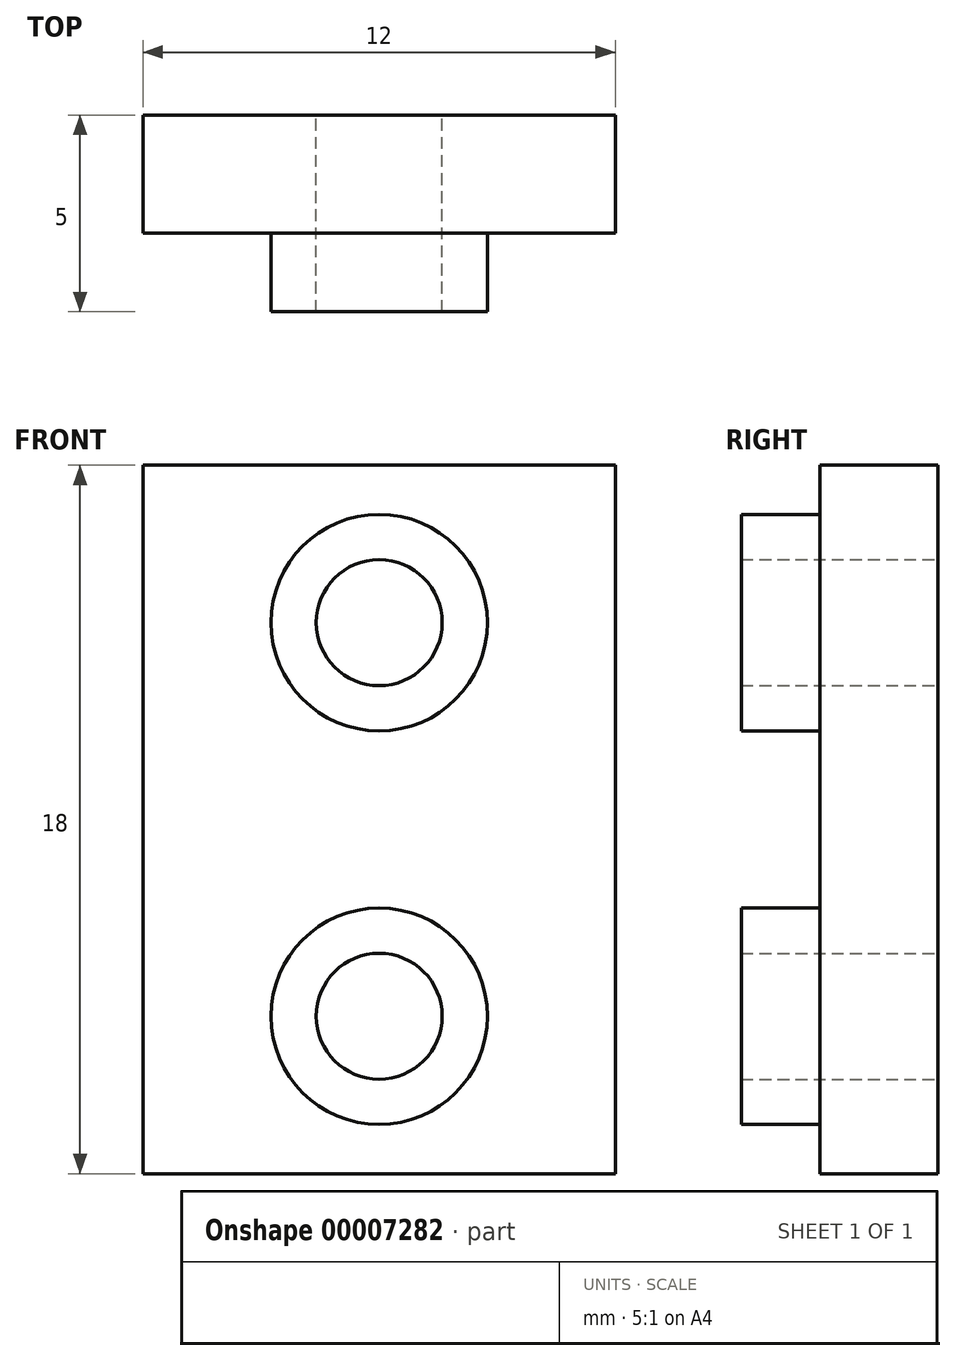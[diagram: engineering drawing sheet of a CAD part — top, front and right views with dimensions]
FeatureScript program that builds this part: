
annotation { "Feature Type Name" : "Feature", "Feature Type Description" : "" }
export const myFeature = defineFeature(function(context is Context, id is Id, definition is map)
    precondition{}
    {
        {
            var Q0;
            Q0=qCreatedBy(makeId("Front.planeOp"),FACE);
            var sketch = newSketch(context, id + "F0", { "sketchPlane" : qUnion([Q0])});
            skLineSegment(sketch, "E0.rect.bottom", {"start": v(6, 9) * mm, "end": v(-6, 9) * mm});
            skLineSegment(sketch, "E0.rect.top", {"start": v(6, -9) * mm, "end": v(-6, -9) * mm});
            skLineSegment(sketch, "E0.rect.left", {"start": v(6, 9) * mm, "end": v(6, -9) * mm});
            skLineSegment(sketch, "E0.rect.right", {"start": v(-6, 9) * mm, "end": v(-6, -9) * mm});
            skPoint(sketch, "E0.rect.middle", {"position": v(0, 0) * mm});
            skCircle(sketch, "E1", {"center": v(0, 5) * mm, "radius": 1.6 * mm});
            skCircle(sketch, "E2", {"center": v(0, -5) * mm, "radius": 1.6 * mm});
            skLineSegment(sketch, "E3", {"start": v(0, 5) * mm, "end": v(0, -5) * mm, "construction": true});
            skSolve(sketch);
        }
        {
            var Q0;
            Q0=makeQuery(id+"F0.imprint","IMPRINT",FACE,{"disambiguationData":[TD([[makeQuery(id+"F0.imprint","IMPRINT",EDGE,{"derivedFrom":sQuery(id+"F0.wireOp",EDGE,"E0.rect.bottom")}),1.0]])]});
            extrude(context, id + "F1", {"entities" : qUnion([Q0]), "depth" : 3 * mm});
        }
        {
            var Q0;
            Q0=makeQuery(id+"F1.opExtrude","CAP_FACE",FACE,{"disambiguationData":[OSD([sQuery(id+"F0.wireOp",EDGE,"E0.rect.bottom"),sQuery(id+"F0.wireOp",EDGE,"E0.rect.top"),sQuery(id+"F0.wireOp",EDGE,"E0.rect.left"),sQuery(id+"F0.wireOp",EDGE,"E0.rect.right"),sQuery(id+"F0.wireOp",EDGE,"E1"),sQuery(id+"F0.wireOp",EDGE,"E2")])],"isStart":false});
            var sketch = newSketch(context, id + "F2", { "sketchPlane" : qUnion([Q0])});
            skCircle(sketch, "E4", {"center": v(0, 5) * mm, "radius": 2.75 * mm});
            skCircle(sketch, "E5", {"center": v(0, -5) * mm, "radius": 2.75 * mm});
            skSolve(sketch);
        }
        {
            var Q0;
            Q0=makeQuery(id+"F2.imprint","IMPRINT",FACE,{"disambiguationData":[TD([[makeQuery(id+"F2.imprint","IMPRINT",EDGE,{"derivedFrom":sQuery(id+"F2.wireOp",EDGE,"E4")}),1.0]])]});
            var Q1;
            Q1=makeQuery(id+"F2.imprint","IMPRINT",FACE,{"disambiguationData":[TD([[makeQuery(id+"F2.imprint","IMPRINT",EDGE,{"derivedFrom":sQuery(id+"F2.wireOp",EDGE,"E5")}),1.0]])]});
            extrude(context, id + "F3", {"entities" : qUnion([Q0, Q1]), "operationType" : NewBodyOperationType.ADD, "depth" : 2 * mm});
        }
    });
